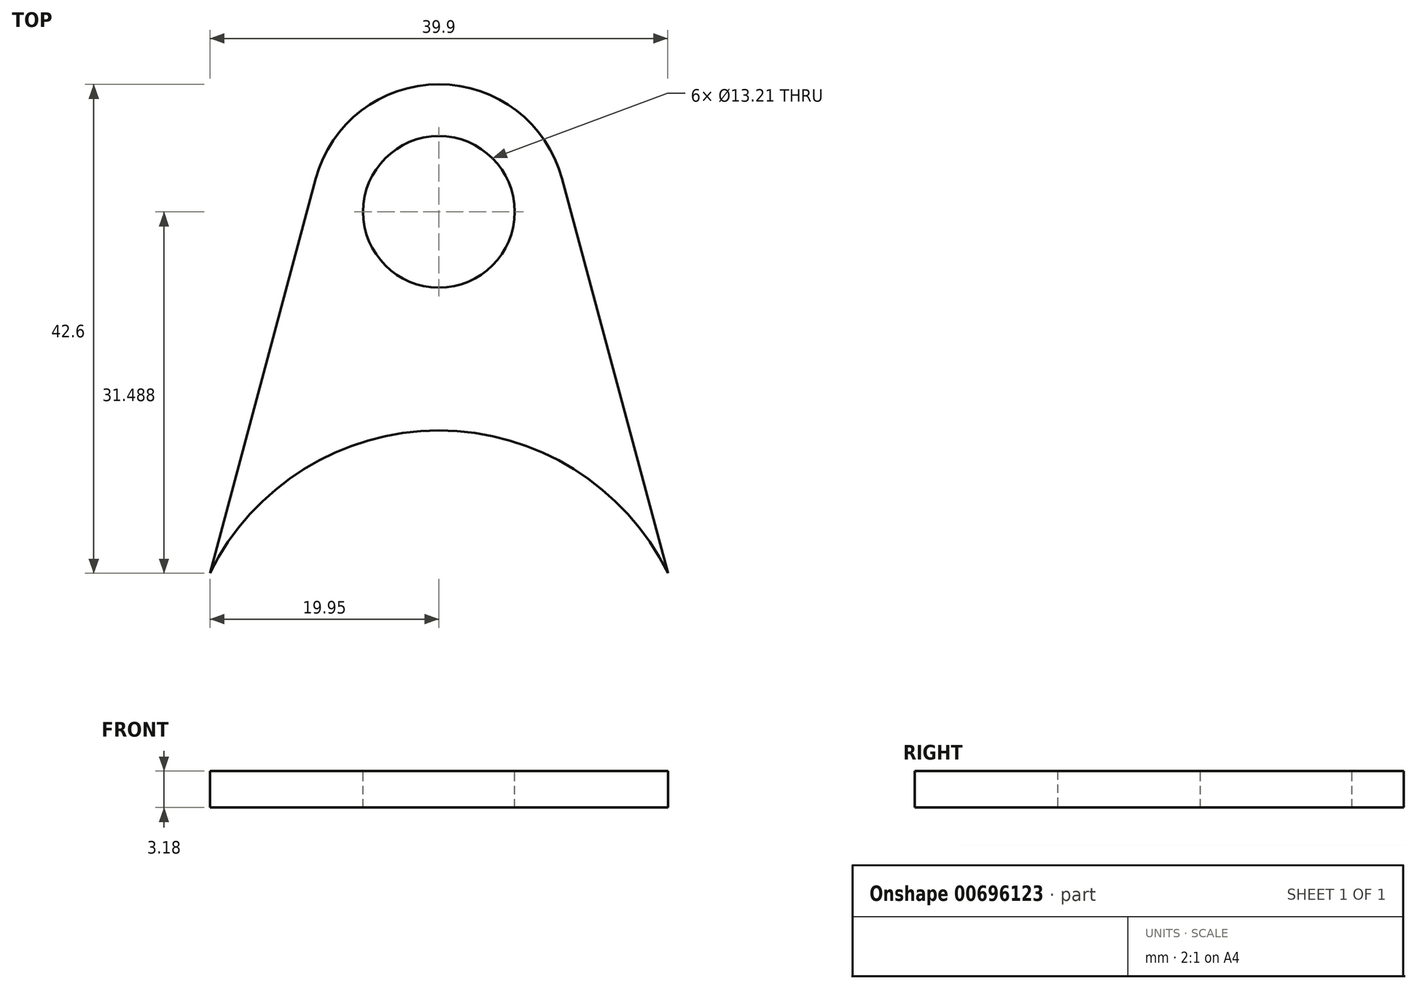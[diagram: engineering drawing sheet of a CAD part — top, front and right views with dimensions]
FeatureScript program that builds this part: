
annotation { "Feature Type Name" : "Feature", "Feature Type Description" : "" }
export const myFeature = defineFeature(function(context is Context, id is Id, definition is map)
    precondition{}
    {
        {
            var Q0;
            Q0=qCreatedBy(makeId("Top.planeOp"),FACE);
            var sketch = newSketch(context, id + "F0", { "sketchPlane" : qUnion([Q0])});
            skLineSegment(sketch, "E0", {"start": v(0, -49.37) * mm, "end": v(0, 65.55) * mm, "construction": true});
            skArc(sketch, "E1", {"start": v(0, 29.22) * mm, "mid": v(-6.76, 26.93) * mm, "end": v(-10.73, 20.99) * mm});
            skArc(sketch, "E2", {"start": v(0, -0.94) * mm, "mid": v(-11.76, -4.3) * mm, "end": v(-19.95, -13.38) * mm});
            skLineSegment(sketch, "E3", {"start": v(-19.95, -13.38) * mm, "end": v(-10.73, 20.99) * mm});
            skArc(sketch, "E4.MirrorCS", {"start": v(0, 29.22) * mm, "mid": v(6.76, 26.93) * mm, "end": v(10.73, 20.99) * mm});
            skLineSegment(sketch, "E5.MirrorCS", {"start": v(19.95, -13.38) * mm, "end": v(10.73, 20.99) * mm});
            skArc(sketch, "E6.MirrorCS", {"start": v(0, -0.94) * mm, "mid": v(11.76, -4.3) * mm, "end": v(19.95, -13.38) * mm});
            skLineSegment(sketch, "E7", {"start": v(19.95, -13.38) * mm, "end": v(19.95, -13.38) * mm});
            skSolve(sketch);
        }
        {
            var Q0;
            Q0=qSketchRegion(id+"F0",true);
            extrude(context, id + "F1", {"entities" : qUnion([Q0]), "depth" : 3.17 * mm, "offsetDistance" : 25.4 * mm});
        }
        {
            var Q0;
            Q0=makeQuery(id+"F1.opExtrude","CAP_FACE",FACE,{"disambiguationData":[OSD([sQuery(id+"F0.wireOp",EDGE,"E1"),sQuery(id+"F0.wireOp",EDGE,"E2"),sQuery(id+"F0.wireOp",EDGE,"E3"),sQuery(id+"F0.wireOp",EDGE,"E4.MirrorCS"),sQuery(id+"F0.wireOp",EDGE,"E5.MirrorCS"),sQuery(id+"F0.wireOp",EDGE,"E6.MirrorCS"),sQuery(id+"F0.wireOp",EDGE,"rgRoUT8c-bVL2-FPYU-7MTc-vp1h9EsBAV6d"),sQuery(id+"F0.wireOp",EDGE,"05189ca0-4bbf-4e7c-aff5-e242d629c5390.MirrorCS")])],"isStart":false});
            var sketch = newSketch(context, id + "F2", { "sketchPlane" : qUnion([Q0])});
            skPoint(sketch, "E8", {"position": v(0, 18.1) * mm});
            skSolve(sketch);
        }
        {
            var Q0;
            Q0=sQuery(id+"F2.wireOp",VERTEX,"E8");
            var Q1;
            Q1=makeQuery(id+"F1.opExtrude","SWEPT_BODY",BODY,{"disambiguationData":[OSD([sQuery(id+"F0.wireOp",EDGE,"E1"),sQuery(id+"F0.wireOp",EDGE,"E2"),sQuery(id+"F0.wireOp",EDGE,"E3"),sQuery(id+"F0.wireOp",EDGE,"E4.MirrorCS"),sQuery(id+"F0.wireOp",EDGE,"E5.MirrorCS"),sQuery(id+"F0.wireOp",EDGE,"E6.MirrorCS"),sQuery(id+"F0.wireOp",EDGE,"rgRoUT8c-bVL2-FPYU-7MTc-vp1h9EsBAV6d"),sQuery(id+"F0.wireOp",EDGE,"05189ca0-4bbf-4e7c-aff5-e242d629c5390.MirrorCS")])]});
            hole(context, id + "F3", {"style" : HoleStyle.SIMPLE, "endStyle" : HoleEndStyle.THROUGH, "holeDiameter" : 13.2 * mm, "isTappedThrough" : true, "tappedDepth" : 12.7 * mm, "tapClearance" : 3, "locations" : qUnion([Q0]), "scope" : qUnion([Q1]), "majorDiameter" : 6.35 * mm});
        }
    });
